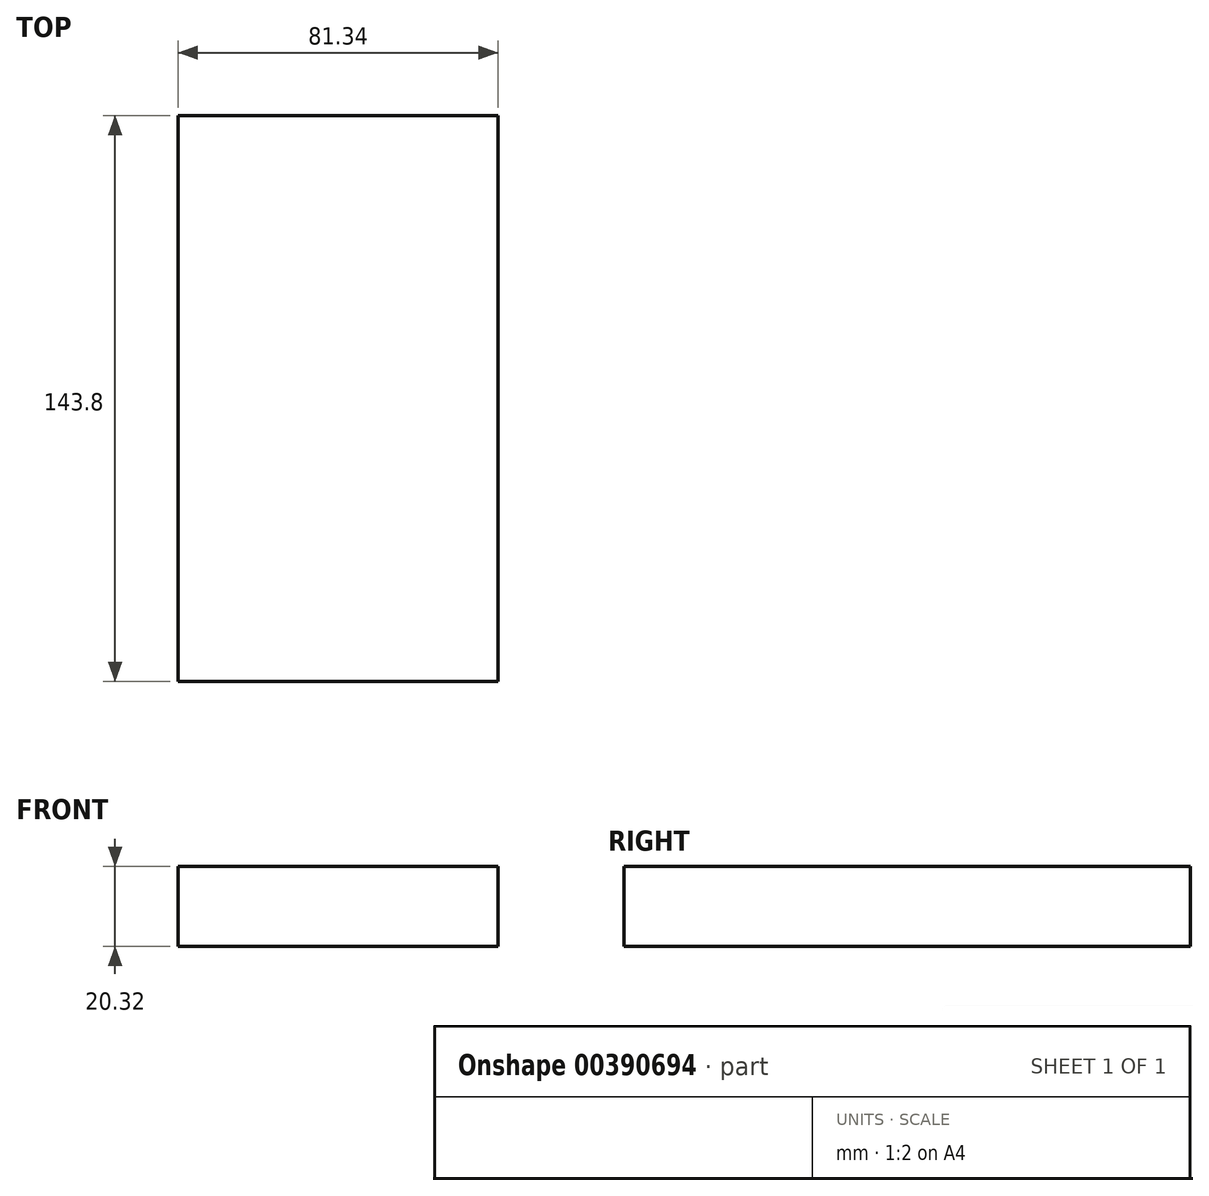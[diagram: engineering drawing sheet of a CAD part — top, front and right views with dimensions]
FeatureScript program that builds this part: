
annotation { "Feature Type Name" : "Feature", "Feature Type Description" : "" }
export const myFeature = defineFeature(function(context is Context, id is Id, definition is map)
    precondition{}
    {
        {
            var Q0;
            Q0=qCreatedBy(makeId("Top.planeOp"),FACE);
            var sketch = newSketch(context, id + "F0", { "sketchPlane" : qUnion([Q0])});
            skLineSegment(sketch, "E0.bottom", {"start": v(40.67, 71.9) * mm, "end": v(-40.67, 71.9) * mm});
            skLineSegment(sketch, "E0.top", {"start": v(40.67, -71.9) * mm, "end": v(-40.67, -71.9) * mm});
            skLineSegment(sketch, "E0.left", {"start": v(40.67, 71.9) * mm, "end": v(40.67, -71.9) * mm});
            skLineSegment(sketch, "E0.right", {"start": v(-40.67, 71.9) * mm, "end": v(-40.67, -71.9) * mm});
            skPoint(sketch, "E0.middle", {"position": v(0, 0) * mm});
            skLineSegment(sketch, "E1.bottom", {"start": v(36.03, 67) * mm, "end": v(-36.03, 67) * mm});
            skLineSegment(sketch, "E1.top", {"start": v(36.03, -67) * mm, "end": v(-36.03, -67) * mm});
            skLineSegment(sketch, "E1.left", {"start": v(36.03, 67) * mm, "end": v(36.03, -67) * mm});
            skLineSegment(sketch, "E1.right", {"start": v(-36.03, 67) * mm, "end": v(-36.03, -67) * mm});
            skSolve(sketch);
        }
        {
            var Q0;
            Q0 = qSketchRegion(id + "F0", true);
            extrude(context, id + "F1", {"entities" : qUnion([Q0]), "oppositeDirection" : true, "depth" : 20.32 * mm});
        }
        {
            var Q0;
            Q0=makeQuery(id+"F1.opExtrude","SWEPT_FACE",FACE,{"disambiguationData":[OSD([sQuery(id+"F0.wireOp",EDGE,"E0.top")])]});
            var sketch = newSketch(context, id + "F2", { "sketchPlane" : qUnion([Q0])});
            skSolve(sketch);
        }
        {
            var Q0;
            Q0 = qSketchRegion(id + "F2", true);
            var Q1;
            {var subQ0=sQuery(id+"F0.wireOp",EDGE,"E0.top");Q1=makeQuery(id+"F2.imprint","IMPRINT",FACE,{"disambiguationData":[TD([[makeQuery(id+"F2.imprint","IMPRINT",EDGE,{"derivedFrom":makeQuery(id+"F1.opExtrude","CAP_EDGE",EDGE,{"disambiguationData":[OSD([subQ0])],"isStart":true})}),1.0]])]});}
            extrude(context, id + "F3", {"entities" : qUnion([Q0, Q1]), "operationType" : NewBodyOperationType.ADD, "oppositeDirection" : true, "depth" : 139.7 * mm});
        }
        {
            var Q0;
            {var subQ0=sQuery(id+"F0.wireOp",EDGE,"E0.top");Q0=makeQuery(id+"F3.boolean.opBoolean","MERGE",FACE,{"derivedFrom":[makeQuery(id+"F1.opExtrude","CAP_FACE",FACE,{"disambiguationData":[OSD([sQuery(id+"F0.wireOp",EDGE,"E0.bottom"),subQ0,sQuery(id+"F0.wireOp",EDGE,"E0.left"),sQuery(id+"F0.wireOp",EDGE,"E0.right"),sQuery(id+"F0.wireOp",EDGE,"E1.bottom"),sQuery(id+"F0.wireOp",EDGE,"E1.top"),sQuery(id+"F0.wireOp",EDGE,"E1.left"),sQuery(id+"F0.wireOp",EDGE,"E1.right")])],"isStart":true}),makeQuery(id+"F3.opExtrude","SWEPT_FACE",FACE,{"disambiguationData":[OSD([subQ0]),TDD([makeQuery(id+"F2.imprint","IMPRINT",EDGE,{"derivedFrom":makeQuery(id+"F1.opExtrude","CAP_EDGE",EDGE,{"disambiguationData":[OSD([subQ0])],"isStart":true})})])]})]});}
            var sketch = newSketch(context, id + "F4", { "sketchPlane" : qUnion([Q0])});
            skLineSegment(sketch, "E2.bottom", {"start": v(-40.67, 71.9) * mm, "end": v(40.67, 71.9) * mm});
            skLineSegment(sketch, "E2.top", {"start": v(-40.67, 65.46) * mm, "end": v(40.67, 65.46) * mm});
            skLineSegment(sketch, "E2.left", {"start": v(-40.67, 71.9) * mm, "end": v(-40.67, 65.46) * mm});
            skLineSegment(sketch, "E2.right", {"start": v(40.67, 71.9) * mm, "end": v(40.67, 65.46) * mm});
            skSolve(sketch);
        }
        {
            var Q0;
            Q0=sQuery(id+"F4.wireOp",EDGE,"E2.top");
            extrude(context, id + "F5", {"bodyType" : ToolBodyType.SURFACE, "surfaceEntities" : qUnion([Q0]), "depth" : 67.96 * mm});
        }
    });
